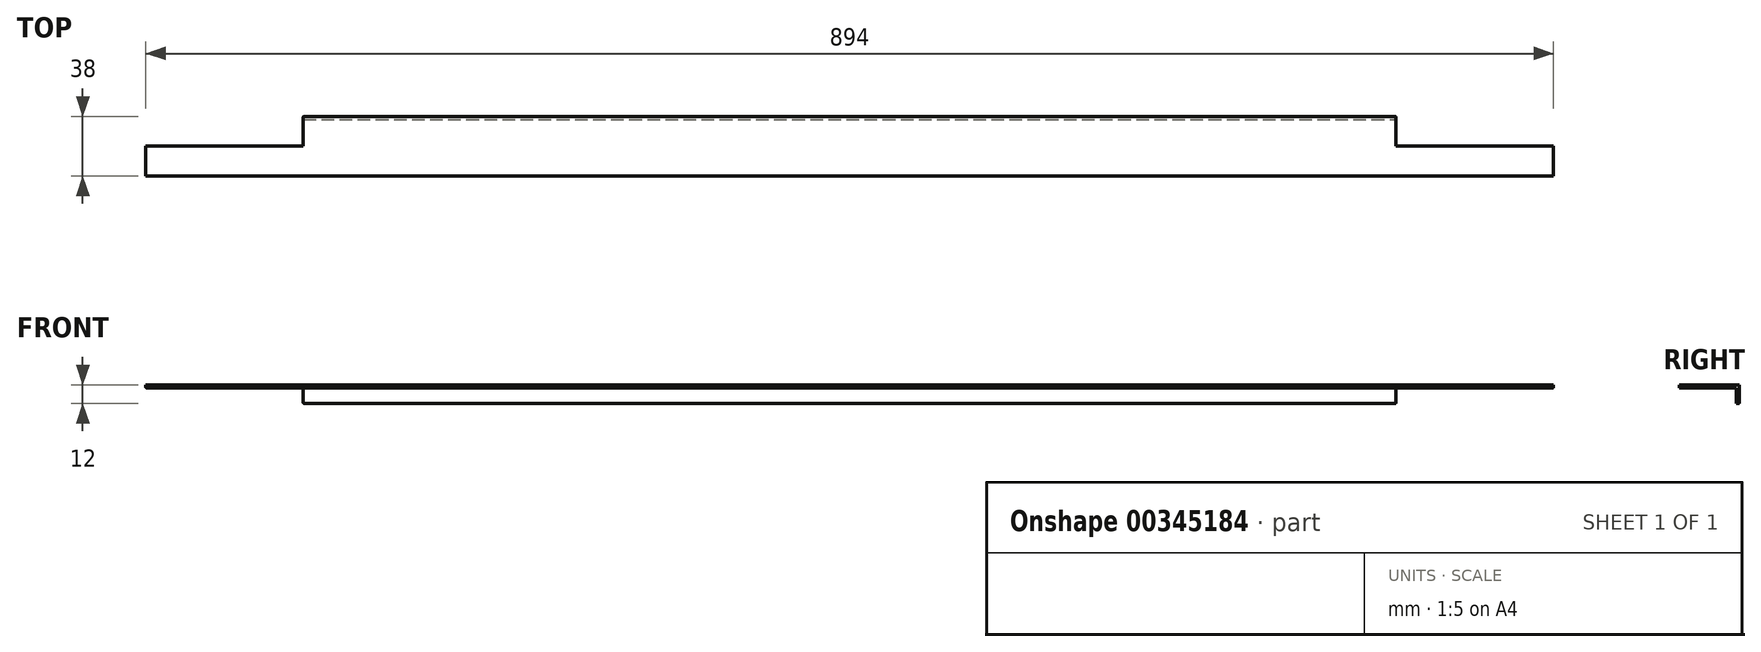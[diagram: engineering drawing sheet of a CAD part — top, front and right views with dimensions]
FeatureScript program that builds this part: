
annotation { "Feature Type Name" : "Feature", "Feature Type Description" : "" }
export const myFeature = defineFeature(function(context is Context, id is Id, definition is map)
    precondition{}
    {
        {
            var Q0;
            Q0=qCreatedBy(makeId("Front.planeOp"),FACE);
            var sketch = newSketch(context, id + "F0", { "sketchPlane" : qUnion([Q0])});
            skLineSegment(sketch, "E0.bottom", {"start": v(0, 0) * mm, "end": v(-50.16, 0) * mm});
            skLineSegment(sketch, "E0.top", {"start": v(0, 16.6) * mm, "end": v(-50.16, 16.6) * mm});
            skLineSegment(sketch, "E0.left", {"start": v(0, 0) * mm, "end": v(0, 16.6) * mm});
            skLineSegment(sketch, "E0.right", {"start": v(-50.16, 0) * mm, "end": v(-50.16, 16.6) * mm});
            skSolve(sketch);
        }
        {
            var Q0;
            Q0=makeQuery(id+"F0.imprint","IMPRINT",FACE,{"disambiguationData":[TD([[makeQuery(id+"F0.imprint","IMPRINT",EDGE,{"derivedFrom":sQuery(id+"F0.wireOp",EDGE,"E0.bottom")}),-1.0]])]});
            extrude(context, id + "F1", {"entities" : qUnion([Q0]), "oppositeDirection" : true, "depth" : 38 * mm});
        }
        {
            var Q0;
            Q0=makeQuery(id+"F1.opExtrude","SWEPT_FACE",FACE,{"disambiguationData":[OSD([sQuery(id+"F0.wireOp",EDGE,"E0.bottom")])]});
            extrude(context, id + "F2", {"entities" : qUnion([Q0]), "operationType" : NewBodyOperationType.INTERSECT, "oppositeDirection" : true, "depth" : 2 * mm});
        }
        {
            var Q0;
            Q0=makeQuery(id+"F1.opExtrude","SWEPT_FACE",FACE,{"disambiguationData":[OSD([sQuery(id+"F0.wireOp",EDGE,"E0.left")])]});
            extrude(context, id + "F3", {"entities" : qUnion([Q0]), "operationType" : NewBodyOperationType.ADD, "oppositeDirection" : true, "depth" : 894 * mm});
        }
        {
            var Q0;
            Q0=makeQuery(id+"F1.opExtrude","SWEPT_FACE",FACE,{"disambiguationData":[OSD([sQuery(id+"F0.wireOp",EDGE,"E0.left")])]});
            var sketch = newSketch(context, id + "F4", { "sketchPlane" : qUnion([Q0])});
            skLineSegment(sketch, "E1", {"start": v(19, 2) * mm, "end": v(19, 0) * mm});
            skSolve(sketch);
        }
        {
            var Q0;
            {var subQ0=sQuery(id+"F4.wireOp",EDGE,"E1");Q0=makeQuery(id+"F4.imprint","IMPRINT",FACE,{"disambiguationData":[TD([[makeQuery(id+"F4.imprint","IMPRINT",EDGE,{"derivedFrom":subQ0}),1.0]])]});}
            extrude(context, id + "F5", {"entities" : qUnion([Q0]), "operationType" : NewBodyOperationType.REMOVE, "oppositeDirection" : true, "depth" : 100 * mm});
        }
        {
            var Q0;
            Q0=makeQuery(id+"F3.opExtrude","CAP_FACE",FACE,{"disambiguationData":[OSD([sQuery(id+"F0.wireOp",EDGE,"E0.left")])],"isStart":false});
            var sketch = newSketch(context, id + "F6", { "sketchPlane" : qUnion([Q0])});
            skLineSegment(sketch, "E2", {"start": v(-19, 2) * mm, "end": v(-19, 0) * mm});
            skSolve(sketch);
        }
        {
            var Q0;
            {var subQ0=sQuery(id+"F6.wireOp",EDGE,"E2");Q0=makeQuery(id+"F6.imprint","IMPRINT",FACE,{"disambiguationData":[TD([[makeQuery(id+"F6.imprint","IMPRINT",EDGE,{"derivedFrom":subQ0}),-1.0]])]});}
            extrude(context, id + "F7", {"entities" : qUnion([Q0]), "operationType" : NewBodyOperationType.REMOVE, "oppositeDirection" : true, "depth" : 100 * mm});
        }
        {
            var Q0;
            {var subQ0=sQuery(id+"F0.wireOp",EDGE,"E0.left");var subQ1=sQuery(id+"F0.wireOp",EDGE,"E0.bottom");Q0=makeQuery(id+"F3.boolean.opBoolean","MERGE",FACE,{"derivedFrom":[makeQuery(id+"F1.opExtrude","SWEPT_FACE",FACE,{"disambiguationData":[OSD([subQ1])]}),makeQuery(id+"F3.opExtrude","SWEPT_FACE",FACE,{"disambiguationData":[OSD([subQ1,subQ0]),TDD([makeQuery(id+"F1.opExtrude","SWEPT_EDGE",EDGE,{"disambiguationData":[OSD([subQ1,subQ0])]})])]})]});}
            var sketch = newSketch(context, id + "F8", { "sketchPlane" : qUnion([Q0])});
            skLineSegment(sketch, "E3.bottom", {"start": v(-794, -38) * mm, "end": v(-100, -38) * mm});
            skLineSegment(sketch, "E3.top", {"start": v(-794, -28.5) * mm, "end": v(-100, -28.5) * mm});
            skLineSegment(sketch, "E3.left", {"start": v(-794, -38) * mm, "end": v(-794, -28.5) * mm});
            skLineSegment(sketch, "E3.right", {"start": v(-100, -38) * mm, "end": v(-100, -28.5) * mm});
            skSolve(sketch);
        }
        {
            var Q0;
            Q0=makeQuery(id+"F8.imprint","IMPRINT",FACE,{"disambiguationData":[TD([[makeQuery(id+"F8.imprint","IMPRINT",EDGE,{"derivedFrom":sQuery(id+"F8.wireOp",EDGE,"E3.bottom")}),-1.0]])]});
            extrude(context, id + "F9", {"entities" : qUnion([Q0]), "operationType" : NewBodyOperationType.ADD, "depth" : 10 * mm});
        }
        {
            var Q0;
            Q0=makeQuery(id+"F9.opExtrude","SWEPT_FACE",FACE,{"disambiguationData":[OSD([sQuery(id+"F8.wireOp",EDGE,"E3.top")])]});
            extrude(context, id + "F10", {"entities" : qUnion([Q0]), "operationType" : NewBodyOperationType.REMOVE, "oppositeDirection" : true, "depth" : 7.5 * mm});
        }
        {
            var Q0;
            {var subQ0=sQuery(id+"F0.wireOp",EDGE,"E0.left");var subQ1=sQuery(id+"F0.wireOp",EDGE,"E0.bottom");Q0=makeQuery(id+"F3.opExtrude","CAP_EDGE",EDGE,{"disambiguationData":[OSD([subQ1,subQ0]),TDD([makeQuery(id+"F2.boolean.opBoolean","COPY",EDGE,{"derivedFrom":makeQuery(id+"F2.boolean.toolComplement.opBoolean","COPY",EDGE,{"derivedFrom":makeQuery(id+"F2.opExtrude","CAP_EDGE",EDGE,{"disambiguationData":[OSD([subQ1,subQ0])],"isStart":false})})})])],"isStart":false});}
            var Q1;
            {var subQ0=sQuery(id+"F0.wireOp",EDGE,"E0.left");var subQ1=sQuery(id+"F0.wireOp",EDGE,"E0.bottom");Q1=makeQuery(id+"F3.opExtrude","CAP_EDGE",EDGE,{"disambiguationData":[OSD([subQ1,subQ0]),TDD([makeQuery(id+"F1.opExtrude","SWEPT_EDGE",EDGE,{"disambiguationData":[OSD([subQ1,subQ0])]})])],"isStart":false});}
            var Q2;
            {var subQ0=sQuery(id+"F6.wireOp",EDGE,"E2");var subQ1=sQuery(id+"F0.wireOp",EDGE,"E0.left");var subQ2=sQuery(id+"F0.wireOp",EDGE,"E0.bottom");Q2=makeQuery(id+"F7.boolean.opBoolean","COPY",EDGE,{"derivedFrom":makeQuery(id+"F7.opExtrude","SWEPT_EDGE",EDGE,{"disambiguationData":[OSD([subQ2,subQ1,subQ0]),TDD([makeQuery(id+"F6.imprint","INTERSECT",VERTEX,{"derivedFrom":[makeQuery(id+"F3.opExtrude","CAP_EDGE",EDGE,{"disambiguationData":[OSD([subQ2,subQ1]),TDD([makeQuery(id+"F2.boolean.opBoolean","COPY",EDGE,{"derivedFrom":makeQuery(id+"F2.boolean.toolComplement.opBoolean","COPY",EDGE,{"derivedFrom":makeQuery(id+"F2.opExtrude","CAP_EDGE",EDGE,{"disambiguationData":[OSD([subQ2,subQ1])],"isStart":false})})})])],"isStart":false}),subQ0]})])]})});}
            var Q3;
            {var subQ0=sQuery(id+"F6.wireOp",EDGE,"E2");var subQ1=sQuery(id+"F0.wireOp",EDGE,"E0.left");var subQ2=sQuery(id+"F0.wireOp",EDGE,"E0.bottom");Q3=makeQuery(id+"F7.boolean.opBoolean","COPY",EDGE,{"derivedFrom":makeQuery(id+"F7.opExtrude","SWEPT_EDGE",EDGE,{"disambiguationData":[OSD([subQ2,subQ1,subQ0]),TDD([makeQuery(id+"F6.imprint","INTERSECT",VERTEX,{"derivedFrom":[makeQuery(id+"F3.opExtrude","CAP_EDGE",EDGE,{"disambiguationData":[OSD([subQ2,subQ1]),TDD([makeQuery(id+"F1.opExtrude","SWEPT_EDGE",EDGE,{"disambiguationData":[OSD([subQ2,subQ1])]})])],"isStart":false}),subQ0]})])]})});}
            var Q4;
            {var subQ0=sQuery(id+"F0.wireOp",EDGE,"E0.left");var subQ1=sQuery(id+"F0.wireOp",EDGE,"E0.bottom");var subQ2=makeQuery(id+"F3.opExtrude","CAP_EDGE",EDGE,{"disambiguationData":[OSD([subQ1,subQ0]),TDD([makeQuery(id+"F2.boolean.opBoolean","COPY",EDGE,{"derivedFrom":makeQuery(id+"F2.boolean.toolComplement.opBoolean","COPY",EDGE,{"derivedFrom":makeQuery(id+"F2.opExtrude","CAP_EDGE",EDGE,{"disambiguationData":[OSD([subQ1,subQ0])],"isStart":false})})})])],"isStart":false});Q4=makeQuery(id+"F7.boolean.opBoolean","COPY",EDGE,{"derivedFrom":makeQuery(id+"F7.opExtrude","CAP_EDGE",EDGE,{"disambiguationData":[OSD([subQ1,subQ0]),TDD([makeQuery(id+"F6.imprint","IMPRINT",EDGE,{"disambiguationData":[TD([[makeQuery(id+"F6.imprint","INTERSECT",VERTEX,{"derivedFrom":[subQ2,sQuery(id+"F6.wireOp",EDGE,"E2")]}),1.0]])],"derivedFrom":subQ2})])],"isStart":false})});}
            var Q5;
            {var subQ0=sQuery(id+"F8.wireOp",EDGE,"E3.left");var subQ1=sQuery(id+"F8.wireOp",EDGE,"E3.top");var subQ2=sQuery(id+"F0.wireOp",EDGE,"E0.left");var subQ3=sQuery(id+"F0.wireOp",EDGE,"E0.bottom");var subQ4=makeQuery(id+"F3.opExtrude","CAP_EDGE",EDGE,{"disambiguationData":[OSD([subQ3,subQ2]),TDD([makeQuery(id+"F1.opExtrude","SWEPT_EDGE",EDGE,{"disambiguationData":[OSD([subQ3,subQ2])]})])],"isStart":false});Q5=makeQuery(id+"F10.boolean.opBoolean","MERGE",EDGE,{"derivedFrom":[makeQuery(id+"F7.boolean.opBoolean","COPY",EDGE,{"derivedFrom":makeQuery(id+"F7.opExtrude","CAP_EDGE",EDGE,{"disambiguationData":[OSD([subQ3,subQ2]),TDD([makeQuery(id+"F6.imprint","IMPRINT",EDGE,{"disambiguationData":[TD([[makeQuery(id+"F6.imprint","INTERSECT",VERTEX,{"derivedFrom":[subQ4,sQuery(id+"F6.wireOp",EDGE,"E2")]}),1.0]])],"derivedFrom":subQ4})])],"isStart":false})}),makeQuery(id+"F10.opExtrude","SWEPT_EDGE",EDGE,{"disambiguationData":[OSD([subQ3,subQ2,subQ1,subQ0]),TDD([makeQuery(id+"F9.opExtrude","CAP_VERTEX",VERTEX,{"disambiguationData":[OSD([subQ3,subQ2,subQ1,subQ0])],"isStart":true})])]})]});}
            var Q6;
            Q6=makeQuery(id+"F9.boolean.opBoolean","MERGE",EDGE,{"derivedFrom":[makeQuery(id+"F7.boolean.opBoolean","COPY",EDGE,{"derivedFrom":makeQuery(id+"F7.opExtrude","CAP_EDGE",EDGE,{"disambiguationData":[OSD([sQuery(id+"F0.wireOp",EDGE,"E0.left")])],"isStart":false})}),makeQuery(id+"F9.opExtrude","SWEPT_EDGE",EDGE,{"disambiguationData":[OSD([sQuery(id+"F8.wireOp",EDGE,"E3.bottom"),sQuery(id+"F8.wireOp",EDGE,"E3.left")])]})]});
            var Q7;
            Q7=makeQuery(id+"F10.boolean.opBoolean","COPY",EDGE,{"derivedFrom":makeQuery(id+"F10.opExtrude","CAP_EDGE",EDGE,{"disambiguationData":[OSD([sQuery(id+"F0.wireOp",EDGE,"E0.bottom"),sQuery(id+"F0.wireOp",EDGE,"E0.left"),sQuery(id+"F8.wireOp",EDGE,"E3.top"),sQuery(id+"F8.wireOp",EDGE,"E3.left")])],"isStart":false})});
            var Q8;
            Q8=makeQuery(id+"F9.opExtrude","CAP_EDGE",EDGE,{"disambiguationData":[OSD([sQuery(id+"F8.wireOp",EDGE,"E3.left")])],"isStart":false});
            var Q9;
            Q9=makeQuery(id+"F9.opExtrude","CAP_EDGE",EDGE,{"disambiguationData":[OSD([sQuery(id+"F8.wireOp",EDGE,"E3.bottom")])],"isStart":false});
            var Q10;
            {var subQ0=sQuery(id+"F0.wireOp",EDGE,"E0.left");var subQ1=sQuery(id+"F0.wireOp",EDGE,"E0.bottom");Q10=makeQuery(id+"F3.boolean.opBoolean","MERGE",EDGE,{"derivedFrom":[makeQuery(id+"F2.boolean.opBoolean","COPY",EDGE,{"derivedFrom":makeQuery(id+"F2.boolean.toolComplement.opBoolean","COPY",EDGE,{"derivedFrom":makeQuery(id+"F2.opExtrude","CAP_EDGE",EDGE,{"disambiguationData":[OSD([subQ1]),TDD([makeQuery(id+"F1.opExtrude","CAP_EDGE",EDGE,{"disambiguationData":[OSD([subQ1])],"isStart":false})])],"isStart":false})})}),makeQuery(id+"F3.opExtrude","SWEPT_EDGE",EDGE,{"disambiguationData":[OSD([subQ1,subQ0]),TDD([makeQuery(id+"F2.boolean.opBoolean","COPY",VERTEX,{"derivedFrom":makeQuery(id+"F2.boolean.toolComplement.opBoolean","COPY",VERTEX,{"derivedFrom":makeQuery(id+"F2.opExtrude","CAP_VERTEX",VERTEX,{"disambiguationData":[OSD([subQ1,subQ0]),TDD([makeQuery(id+"F1.opExtrude","CAP_VERTEX",VERTEX,{"disambiguationData":[OSD([subQ1,subQ0])],"isStart":false})])],"isStart":false})})})])]})]});}
            var Q11;
            Q11=makeQuery(id+"F2.boolean.opBoolean","COPY",EDGE,{"derivedFrom":makeQuery(id+"F2.boolean.toolComplement.opBoolean","COPY",EDGE,{"derivedFrom":makeQuery(id+"F2.opExtrude","CAP_EDGE",EDGE,{"disambiguationData":[OSD([sQuery(id+"F0.wireOp",EDGE,"E0.bottom"),sQuery(id+"F0.wireOp",EDGE,"E0.left")])],"isStart":false})})});
            var Q12;
            Q12=makeQuery(id+"F1.opExtrude","SWEPT_EDGE",EDGE,{"disambiguationData":[OSD([sQuery(id+"F0.wireOp",EDGE,"E0.bottom"),sQuery(id+"F0.wireOp",EDGE,"E0.left")])]});
            var Q13;
            {var subQ0=sQuery(id+"F4.wireOp",EDGE,"E1");var subQ1=sQuery(id+"F0.wireOp",EDGE,"E0.left");var subQ2=sQuery(id+"F0.wireOp",EDGE,"E0.bottom");Q13=makeQuery(id+"F5.boolean.opBoolean","COPY",EDGE,{"derivedFrom":makeQuery(id+"F5.opExtrude","SWEPT_EDGE",EDGE,{"disambiguationData":[OSD([subQ2,subQ1,subQ0]),TDD([makeQuery(id+"F4.imprint","INTERSECT",VERTEX,{"derivedFrom":[makeQuery(id+"F2.boolean.opBoolean","COPY",EDGE,{"derivedFrom":makeQuery(id+"F2.boolean.toolComplement.opBoolean","COPY",EDGE,{"derivedFrom":makeQuery(id+"F2.opExtrude","CAP_EDGE",EDGE,{"disambiguationData":[OSD([subQ2,subQ1])],"isStart":false})})}),subQ0]})])]})});}
            var Q14;
            {var subQ0=sQuery(id+"F4.wireOp",EDGE,"E1");var subQ1=sQuery(id+"F0.wireOp",EDGE,"E0.left");var subQ2=sQuery(id+"F0.wireOp",EDGE,"E0.bottom");Q14=makeQuery(id+"F5.boolean.opBoolean","COPY",EDGE,{"derivedFrom":makeQuery(id+"F5.opExtrude","SWEPT_EDGE",EDGE,{"disambiguationData":[OSD([subQ2,subQ1,subQ0]),TDD([makeQuery(id+"F4.imprint","INTERSECT",VERTEX,{"derivedFrom":[makeQuery(id+"F1.opExtrude","SWEPT_EDGE",EDGE,{"disambiguationData":[OSD([subQ2,subQ1])]}),subQ0]})])]})});}
            var Q15;
            Q15=makeQuery(id+"F9.boolean.opBoolean","MERGE",EDGE,{"derivedFrom":[makeQuery(id+"F5.boolean.opBoolean","COPY",EDGE,{"derivedFrom":makeQuery(id+"F5.opExtrude","CAP_EDGE",EDGE,{"disambiguationData":[OSD([sQuery(id+"F0.wireOp",EDGE,"E0.left")])],"isStart":false})}),makeQuery(id+"F9.opExtrude","SWEPT_EDGE",EDGE,{"disambiguationData":[OSD([sQuery(id+"F8.wireOp",EDGE,"E3.bottom"),sQuery(id+"F8.wireOp",EDGE,"E3.right")])]})]});
            var Q16;
            Q16=makeQuery(id+"F10.boolean.opBoolean","COPY",EDGE,{"derivedFrom":makeQuery(id+"F10.opExtrude","CAP_EDGE",EDGE,{"disambiguationData":[OSD([sQuery(id+"F0.wireOp",EDGE,"E0.bottom"),sQuery(id+"F0.wireOp",EDGE,"E0.left"),sQuery(id+"F8.wireOp",EDGE,"E3.top"),sQuery(id+"F8.wireOp",EDGE,"E3.right")])],"isStart":false})});
            var Q17;
            Q17=makeQuery(id+"F9.opExtrude","CAP_EDGE",EDGE,{"disambiguationData":[OSD([sQuery(id+"F8.wireOp",EDGE,"E3.right")])],"isStart":false});
            var Q18;
            {var subQ0=sQuery(id+"F8.wireOp",EDGE,"E3.right");var subQ1=sQuery(id+"F8.wireOp",EDGE,"E3.top");var subQ2=sQuery(id+"F0.wireOp",EDGE,"E0.left");var subQ3=sQuery(id+"F0.wireOp",EDGE,"E0.bottom");var subQ4=makeQuery(id+"F1.opExtrude","SWEPT_EDGE",EDGE,{"disambiguationData":[OSD([subQ3,subQ2])]});Q18=makeQuery(id+"F10.boolean.opBoolean","MERGE",EDGE,{"derivedFrom":[makeQuery(id+"F5.boolean.opBoolean","COPY",EDGE,{"derivedFrom":makeQuery(id+"F5.opExtrude","CAP_EDGE",EDGE,{"disambiguationData":[OSD([subQ3,subQ2]),TDD([makeQuery(id+"F4.imprint","IMPRINT",EDGE,{"disambiguationData":[TD([[makeQuery(id+"F4.imprint","INTERSECT",VERTEX,{"derivedFrom":[subQ4,makeQuery(id+"F1.opExtrude","CAP_EDGE",EDGE,{"disambiguationData":[OSD([subQ2])],"isStart":false})]}),-1.0]])],"derivedFrom":subQ4})])],"isStart":false})}),makeQuery(id+"F10.opExtrude","SWEPT_EDGE",EDGE,{"disambiguationData":[OSD([subQ3,subQ2,subQ1,subQ0]),TDD([makeQuery(id+"F9.opExtrude","CAP_VERTEX",VERTEX,{"disambiguationData":[OSD([subQ3,subQ2,subQ1,subQ0])],"isStart":true})])]})]});}
            var Q19;
            {var subQ0=sQuery(id+"F0.wireOp",EDGE,"E0.left");var subQ1=sQuery(id+"F0.wireOp",EDGE,"E0.bottom");var subQ2=makeQuery(id+"F2.boolean.opBoolean","COPY",EDGE,{"derivedFrom":makeQuery(id+"F2.boolean.toolComplement.opBoolean","COPY",EDGE,{"derivedFrom":makeQuery(id+"F2.opExtrude","CAP_EDGE",EDGE,{"disambiguationData":[OSD([subQ1,subQ0])],"isStart":false})})});Q19=makeQuery(id+"F5.boolean.opBoolean","COPY",EDGE,{"derivedFrom":makeQuery(id+"F5.opExtrude","CAP_EDGE",EDGE,{"disambiguationData":[OSD([subQ1,subQ0]),TDD([makeQuery(id+"F4.imprint","IMPRINT",EDGE,{"disambiguationData":[TD([[makeQuery(id+"F4.imprint","INTERSECT",VERTEX,{"derivedFrom":[subQ2,makeQuery(id+"F1.opExtrude","CAP_EDGE",EDGE,{"disambiguationData":[OSD([subQ0])],"isStart":false})]}),-1.0]])],"derivedFrom":subQ2})])],"isStart":false})});}
            fillet(context, id + "F11", {"entities" : qUnion([Q0, Q1, Q2, Q3, Q4, Q5, Q6, Q7, Q8, Q9, Q10, Q11, Q12, Q13, Q14, Q15, Q16, Q17, Q18, Q19]), "radius" : 0.5 * mm, "tangentPropagation" : true, "allowEdgeOverflow" : false});
        }
    });
